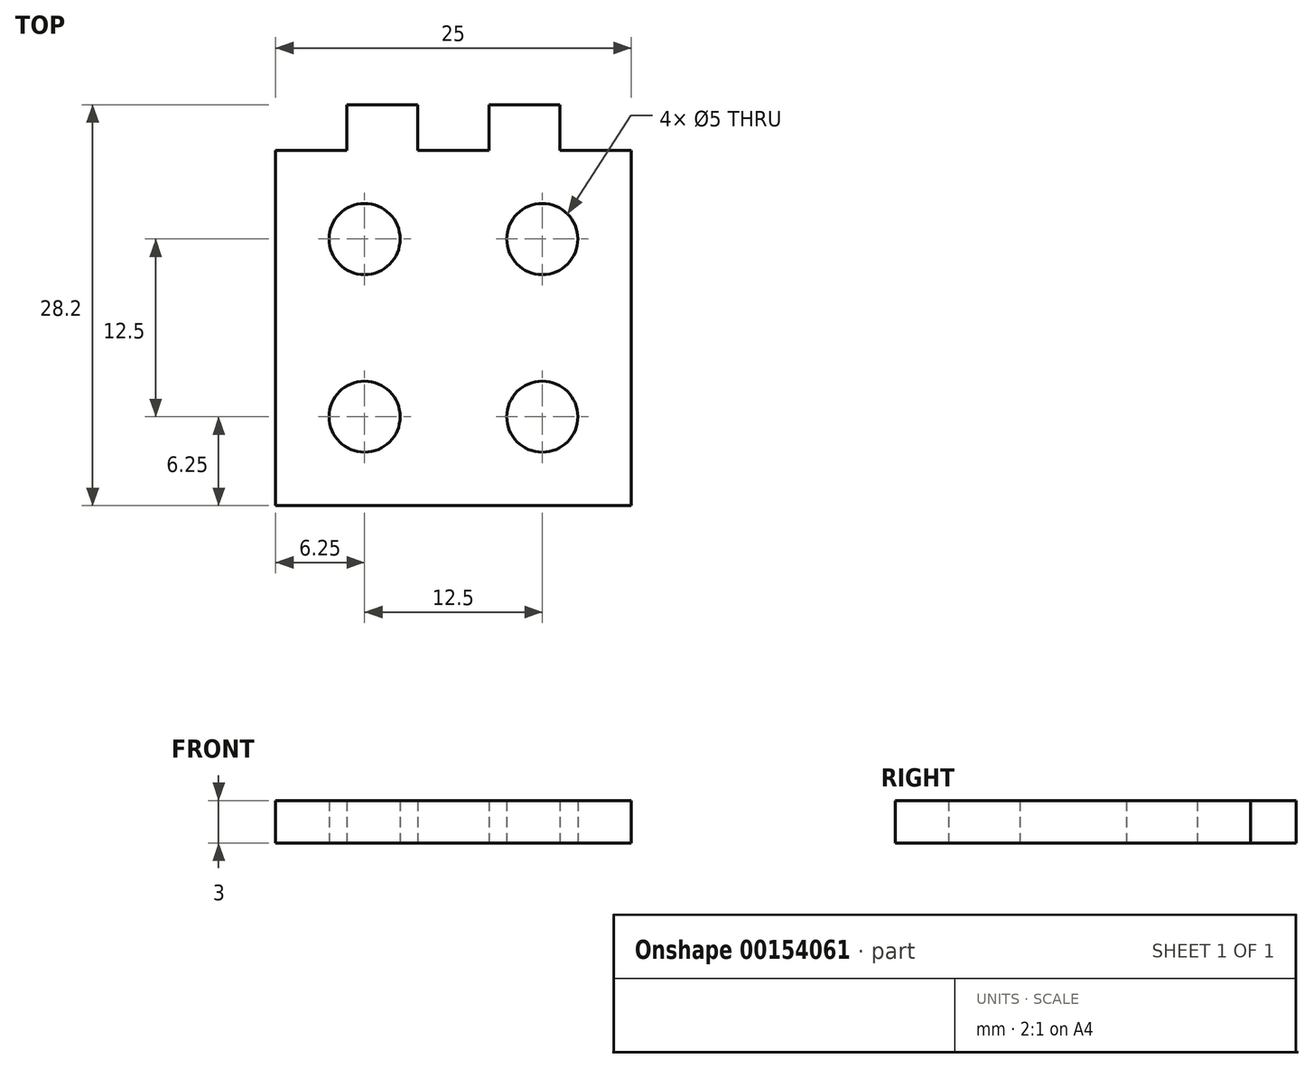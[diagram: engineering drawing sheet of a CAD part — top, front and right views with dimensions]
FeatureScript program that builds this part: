
annotation { "Feature Type Name" : "Feature", "Feature Type Description" : "" }
export const myFeature = defineFeature(function(context is Context, id is Id, definition is map)
    precondition{}
    {
        {
            var Q0;
            Q0=qCreatedBy(makeId("Top.planeOp"),FACE);
            var sketch = newSketch(context, id + "F0", { "sketchPlane" : qUnion([Q0])});
            skLineSegment(sketch, "E0.bottom", {"start": v(12.5, 12.5) * mm, "end": v(7.5, 12.5) * mm});
            skLineSegment(sketch, "E0.top", {"start": v(12.5, -12.5) * mm, "end": v(-12.5, -12.5) * mm});
            skLineSegment(sketch, "E0.left", {"start": v(12.5, 12.5) * mm, "end": v(12.5, -12.5) * mm});
            skLineSegment(sketch, "E0.right", {"start": v(-12.5, 12.5) * mm, "end": v(-12.5, -12.5) * mm});
            skPoint(sketch, "E0.middle", {"position": v(0, 0) * mm});
            skLineSegment(sketch, "E1", {"start": v(-12.5, 12.5) * mm, "end": v(-7.5, 12.5) * mm, "construction": true});
            skLineSegment(sketch, "E2", {"start": v(-7.5, 12.5) * mm, "end": v(-7.5, 15.7) * mm, "construction": true});
            skLineSegment(sketch, "E3", {"start": v(-7.5, 12.5) * mm, "end": v(-7.5, 15.7) * mm});
            skLineSegment(sketch, "E4", {"start": v(-7.5, 15.7) * mm, "end": v(-2.5, 15.7) * mm});
            skLineSegment(sketch, "E5", {"start": v(-2.5, 15.7) * mm, "end": v(-2.5, 12.5) * mm});
            skLineSegment(sketch, "E6", {"start": v(-2.5, 12.5) * mm, "end": v(2.5, 12.5) * mm});
            skLineSegment(sketch, "E7", {"start": v(2.5, 12.5) * mm, "end": v(2.5, 15.7) * mm});
            skLineSegment(sketch, "E8", {"start": v(2.5, 15.7) * mm, "end": v(7.5, 15.7) * mm});
            skLineSegment(sketch, "E9", {"start": v(7.5, 15.7) * mm, "end": v(7.5, 12.5) * mm});
            skLineSegment(sketch, "E10.trimOffspring", {"start": v(-7.5, 12.5) * mm, "end": v(-12.5, 12.5) * mm});
            skLineSegment(sketch, "E11.trimOffspring", {"start": v(2.5, 12.5) * mm, "end": v(-2.5, 12.5) * mm});
            skLineSegment(sketch, "E12", {"start": v(-12.5, -12.5) * mm, "end": v(-12.5, 0) * mm, "construction": true});
            skLineSegment(sketch, "E13", {"start": v(-12.5, -6.25) * mm, "end": v(12.5, -6.25) * mm, "construction": true});
            skLineSegment(sketch, "E14", {"start": v(-12.5, 0) * mm, "end": v(-12.5, 12.5) * mm, "construction": true});
            skLineSegment(sketch, "E15", {"start": v(-12.5, 12.5) * mm, "end": v(0, 12.5) * mm, "construction": true});
            skLineSegment(sketch, "E16", {"start": v(-6.25, 12.5) * mm, "end": v(-6.25, -12.5) * mm, "construction": true});
            skCircle(sketch, "E17", {"center": v(-6.25, -6.25) * mm, "radius": 2.5 * mm});
            skCircle(sketch, "E18.MirrorC", {"center": v(-6.25, 6.25) * mm, "radius": 2.5 * mm});
            skLineSegment(sketch, "E19", {"start": v(0, 12.5) * mm, "end": v(0, -12.5) * mm, "construction": true});
            skCircle(sketch, "E20.MirrorC", {"center": v(6.25, -6.25) * mm, "radius": 2.5 * mm});
            skCircle(sketch, "E21.MirrorC", {"center": v(6.25, 6.25) * mm, "radius": 2.5 * mm});
            skSolve(sketch);
        }
        {
            var Q0;
            Q0=makeQuery(id+"F0.imprint","IMPRINT",FACE,{"disambiguationData":[TD([[makeQuery(id+"F0.imprint","IMPRINT",EDGE,{"derivedFrom":sQuery(id+"F0.wireOp",EDGE,"E0.bottom")}),1.0]])]});
            extrude(context, id + "F1", {"entities" : qUnion([Q0]), "endBound" : BoundingType.SYMMETRIC, "depth" : 3 * mm});
        }
    });
